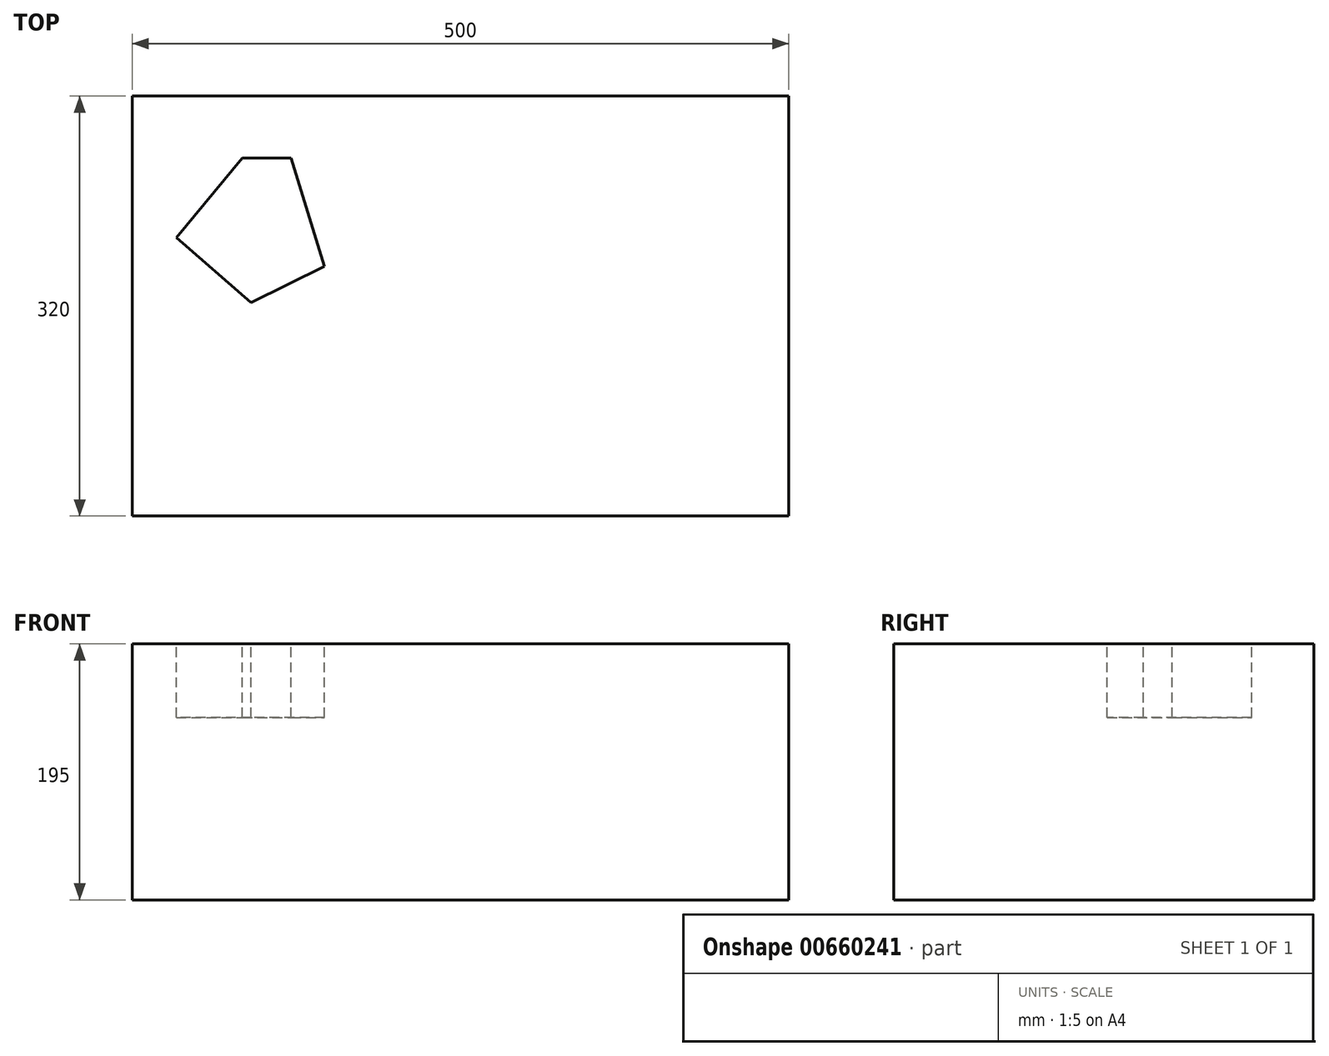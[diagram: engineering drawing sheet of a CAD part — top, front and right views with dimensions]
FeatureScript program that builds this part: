
annotation { "Feature Type Name" : "Feature", "Feature Type Description" : "" }
export const myFeature = defineFeature(function(context is Context, id is Id, definition is map)
    precondition{}
    {
        {
            var Q0;
            Q0=qCreatedBy(makeId("Top.planeOp"),FACE);
            var sketch = newSketch(context, id + "F0", { "sketchPlane" : qUnion([Q0])});
            skLineSegment(sketch, "E0.bottom", {"start": v(-244.46, 69.36) * mm, "end": v(255.54, 69.36) * mm});
            skLineSegment(sketch, "E0.top", {"start": v(-244.46, -250.64) * mm, "end": v(255.54, -250.64) * mm});
            skLineSegment(sketch, "E0.left", {"start": v(-244.46, 69.36) * mm, "end": v(-244.46, -250.64) * mm});
            skLineSegment(sketch, "E0.right", {"start": v(255.54, 69.36) * mm, "end": v(255.54, -250.64) * mm});
            skSolve(sketch);
        }
        {
            var Q0;
            Q0=makeQuery(id+"F0.imprint","IMPRINT",FACE,{"disambiguationData":[TD([[makeQuery(id+"F0.imprint","IMPRINT",EDGE,{"derivedFrom":sQuery(id+"F0.wireOp",EDGE,"E0.bottom")}),-1.0]])]});
            extrude(context, id + "F1", {"entities" : qUnion([Q0]), "oppositeDirection" : true, "depth" : 195 * mm, "offsetDistance" : 25 * mm});
        }
        {
            var Q0;
            Q0=makeQuery(id+"F1.opExtrude","CAP_FACE",FACE,{"disambiguationData":[OSD([sQuery(id+"F0.wireOp",EDGE,"E0.bottom"),sQuery(id+"F0.wireOp",EDGE,"E0.top"),sQuery(id+"F0.wireOp",EDGE,"E0.left"),sQuery(id+"F0.wireOp",EDGE,"E0.right")])],"isStart":true});
            var sketch = newSketch(context, id + "F2", { "sketchPlane" : qUnion([Q0])});
            skLineSegment(sketch, "E1", {"start": v(-160.66, 22.09) * mm, "end": v(-123.48, 22.09) * mm});
            skLineSegment(sketch, "E2", {"start": v(-123.48, 22.09) * mm, "end": v(-97.97, -60.29) * mm});
            skLineSegment(sketch, "E3", {"start": v(-97.97, -60.29) * mm, "end": v(-154.1, -87.99) * mm});
            skLineSegment(sketch, "E4", {"start": v(-154.1, -87.99) * mm, "end": v(-210.96, -38.42) * mm});
            skLineSegment(sketch, "E5", {"start": v(-210.96, -38.42) * mm, "end": v(-160.66, 22.09) * mm});
            skSolve(sketch);
        }
        {
            var Q0;
            Q0=makeQuery(id+"F2.imprint","IMPRINT",FACE,{"disambiguationData":[TD([[makeQuery(id+"F2.imprint","IMPRINT",EDGE,{"derivedFrom":sQuery(id+"F2.wireOp",EDGE,"E1")}),-1.0]])]});
            extrude(context, id + "F3", {"entities" : qUnion([Q0]), "operationType" : NewBodyOperationType.REMOVE, "oppositeDirection" : true, "depth" : 56 * mm, "offsetDistance" : 25 * mm});
        }
    });
